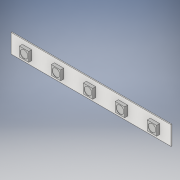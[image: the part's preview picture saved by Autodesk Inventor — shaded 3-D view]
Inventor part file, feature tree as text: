
AUTODESK INVENTOR PART (.ipt)
format: ipt  version: 2019 (Build 230136000, 136)  size: 143,872 bytes
history: native  units: mm
features: extrude x3, sketch x3, pattern_linear x1, projected_geometry x1
ambient origin geometry x8: Origin, YZ Plane, XZ Plane, XY Plane, X Axis, Y Axis, Z Axis, Center Point
bodies: Solid1 (feature_tree)
feature tree (8):
  extrude  "Extrusion1"  Depth=10.0mm
  extrude  "Extrusion2"  Depth=5.0mm
  extrude  "Extrusion3"  Depth=6.0mm
  pattern_linear  "Rectangular Pattern1"  Spacing1=1.6mm  [1 undecoded]
  sketch  "Sketch1"  dims[d0=85.0mm d1=10.0mm]
  sketch  "Sketch2"  dims[d2=0.5mm d3=0.0mm d4=5.0mm]
  sketch  "Sketch3"  dims[d5=5.0mm d6=6.0mm d7=1.6mm d8=0.0mm d9=4.1mm d10=0.1mm d11=0.0mm d12=50.0mm d14=17.0mm]
  projected_geometry  "Projected Loop1"
note: 1 required parameter value undecoded (feature->parameter linkage not recoverable at this tier; creation-order binding heuristic only, values carry confidence <= 0.55)
